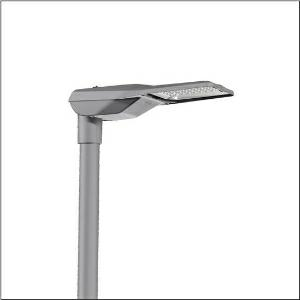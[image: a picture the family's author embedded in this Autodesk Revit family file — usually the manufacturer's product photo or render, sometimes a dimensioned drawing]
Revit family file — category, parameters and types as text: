
# Revit family: streetlight_sl_21_mini___p0_8a_5xe2u33s08gb_2c4a
name_source: partatom
category: Lighting Fixtures
units: mm (PartAtom-declared; Revit-internal decimal feet)

## family parameters
Cut with Voids When Loaded = No
Host = Face
Light Source = No
Part Type = Normal
Room Calculation Point = No
Round Connector Dimension = Use Diameter
Shared = No

## types (1)
- --- (1 x LED, 5990 lm, 40.4 W, 3000K)
    Apparent Load = 40 VA
    CIE Flux Codes = 33 69 96 100 100
    Color Rendering = 70
    Color Temperature = 3000K
    Default Elevation = 1800 mm
    Description = Streetlight SL 21 mini, mast luminaire, primary light control with lens, of PMMA, primary optical cover: cover, of toughened safety glass, transparent, light distribution: P0.8a, light emission: direct distribution, primary light characteristic: asymmetric, installation type: post-top, side-entry, LED, High Power LED, rated luminous flux: 5.990lm, luminous efficacy: 148lm/W, light colour: 730, colour temperature: 3000K, control gear: D4i, control: pre-setting: logarithmic dimming characteristic, flexible luminous flux parameterisation, time-dependent luminous flux control, constant luminous flux control, overheat protection, mains connection: 220..240V, AC, 50/60Hz, start of lifetime: 40W, end of service life: 41W, reduction: 19W, luminaire housing, of diecast aluminium, powder-coated, Siteco® metallic grey (DB 702S), corrosivity category C5 mid according to DIN EN ISO 12944, multi-level sealing system, sealing non-destructively replaceable, inclination adjustable: 0°, 5°, 10°, 15°, please order mast flange separately, length: 628mm, width: 235mm, height: 110mm, mast flange for spigot size: 42mm (side-entry): 5XC10008XM4, 60/48mm (side-entry/post-top): 5XC10108XM2, 76/60mm (side-entry/post-top): 5XC10108XM1, mounting height: 4..8m, Smart Interface above, protection rating (complete): IP66, insulation class (complete): insulation class II (safety insulation), certification: CE, ENEC, ENEC+, VDE, impact resistance: IK10, permissible operating ambient temperature for outdoor applications: -40..+50°C, standard-compliant lighting for roads and squares, packaging unit: 1 piece

Light Distribution: P0.8a
    Height = 110 mm
    Lamp = 1 x LED
    Lamp Light Flux = 5990 lm
    Lamp Power = 40.4 W
    Lamp count = 1
    Length = 625 mm
    Luminous efficacy = 148 lm/W
    Manufacturer = Siteco
    ModVariant = No
    Model = 5XE2U33S08GB
    Number of Poles = 1
    OnlyDefault = Yes
    Power Factor = 1
    Product Name = Streetlight SL 21 mini | P0.8a
    Product group = mast luminaire | pylon top
    ProductGroupID = 6100
    Protection Class = Protection class II
    Protection Degree = IP 66
    RLX_Detail_Level = 1
    RLX_Emergency_Light_Flux = 0 lm
    RLX_Emergency_Type = 0
    RLX_Emergency_Type_DB = No
    RlxData = <blob elided: 25901 chars, md5=c333d742>
    Socket = socket
    Standby Power = 0 W
    System Light Flux = 5990 lm
    System Power = 40 W
    Type Comments = factory setting: luminous flux: 100 % | dim-lin: 254 | 812 mA
    Type Image = l_1003515.jpg
    URL = http://relux.com
    VarID = @adj_072250
    Voltage = 0 V
    Weight = 0.00 kg
    Width = 234 mm

## geometry (parser evidence)
native form markers: Blend x4, Sweep x12
no freeform markers — native parametric forms only
